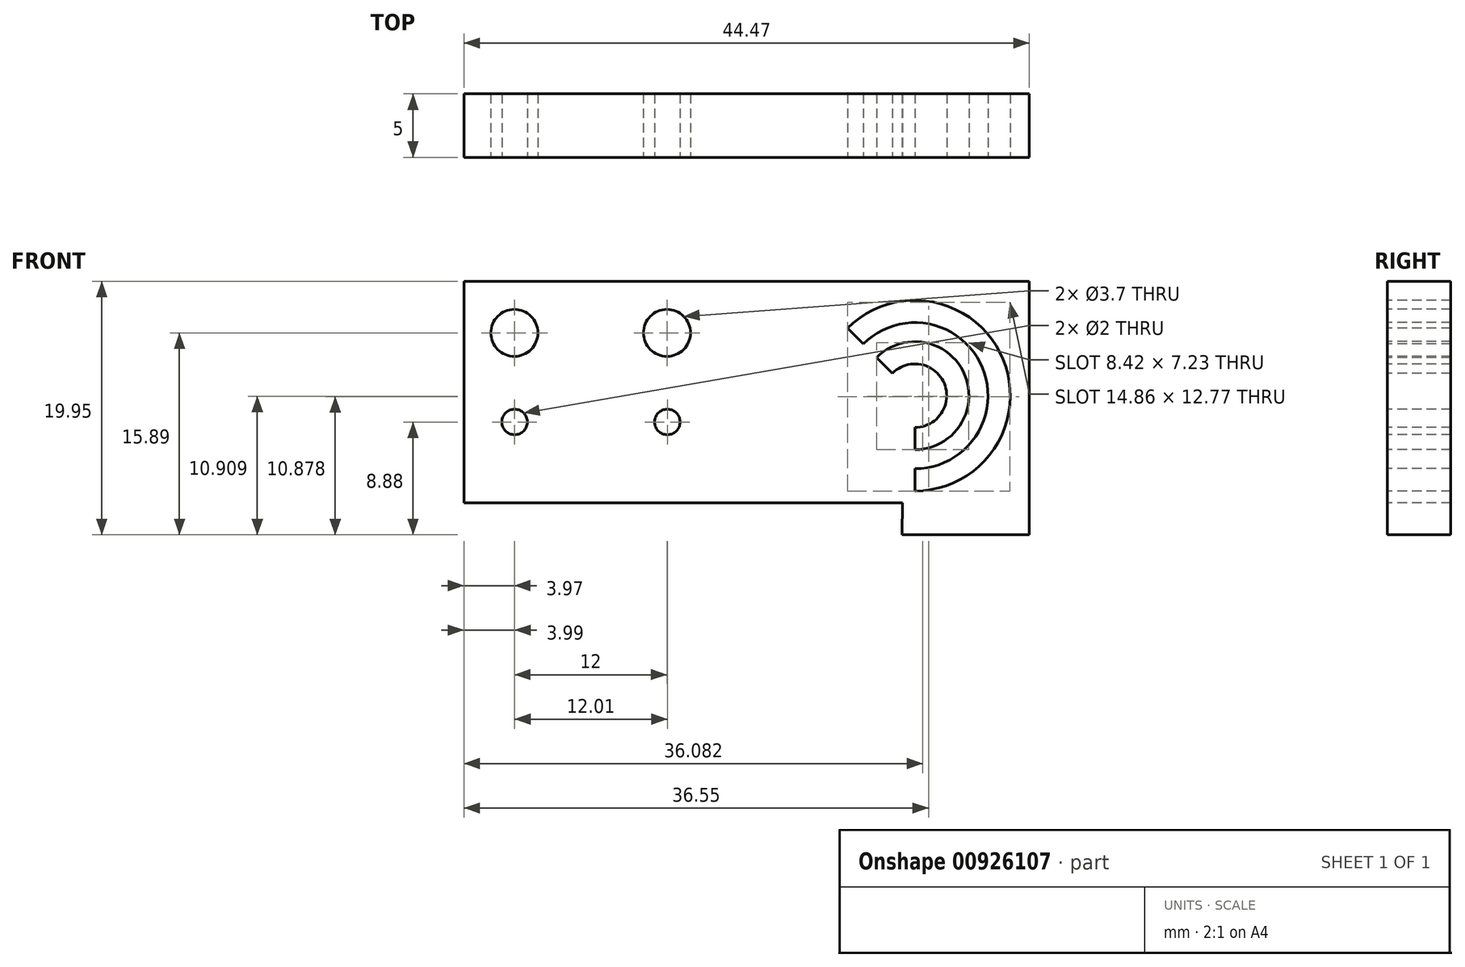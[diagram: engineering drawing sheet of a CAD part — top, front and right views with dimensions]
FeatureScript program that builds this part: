
annotation { "Feature Type Name" : "Feature", "Feature Type Description" : "" }
export const myFeature = defineFeature(function(context is Context, id is Id, definition is map)
    precondition{}
    {
        {
            var Q0;
            Q0=qCreatedBy(makeId("Front.planeOp"),FACE);
            var sketch = newSketch(context, id + "F0", { "sketchPlane" : qUnion([Q0])});
            skLineSegment(sketch, "E0", {"start": v(10, 19.95) * mm, "end": v(-34.47, 19.95) * mm});
            skLineSegment(sketch, "E1", {"start": v(-34.47, 2.5) * mm, "end": v(0.02, 2.5) * mm});
            skLineSegment(sketch, "E2", {"start": v(10, 19.95) * mm, "end": v(10, 0) * mm});
            skLineSegment(sketch, "E3", {"start": v(10, 0) * mm, "end": v(0, 0) * mm});
            skLineSegment(sketch, "E4", {"start": v(0, 0) * mm, "end": v(0.02, 2.5) * mm});
            skCircle(sketch, "E5", {"center": v(-30.5, 15.89) * mm, "radius": 1.85 * mm});
            skLineSegment(sketch, "E6", {"start": v(-34.47, 19.95) * mm, "end": v(-34.47, 2.5) * mm});
            skCircle(sketch, "E7", {"center": v(-18.5, 15.89) * mm, "radius": 1.85 * mm});
            skLineSegment(sketch, "E8", {"start": v(-34.47, 2.5) * mm, "end": v(-30.48, 2.5) * mm});
            skCircle(sketch, "E9", {"center": v(-30.48, 8.88) * mm, "radius": 1 * mm});
            skCircle(sketch, "E10", {"center": v(-18.47, 8.88) * mm, "radius": 1 * mm});
            skLineSegment(sketch, "E11", {"start": v(10, 19.95) * mm, "end": v(1, 19.95) * mm});
            skLineSegment(sketch, "E12", {"start": v(1, 19.95) * mm, "end": v(1, 10.95) * mm});
            skArc(sketch, "E13", {"start": v(1, 8.45) * mm, "mid": v(3.3, 11.9) * mm, "end": v(-0.77, 12.72) * mm});
            skArc(sketch, "E14", {"start": v(1, 6.7) * mm, "mid": v(4.93, 12.58) * mm, "end": v(-2, 13.96) * mm});
            skArc(sketch, "E15", {"start": v(1, 5.2) * mm, "mid": v(6.31, 13.15) * mm, "end": v(-3.07, 15.02) * mm});
            skArc(sketch, "E16", {"start": v(1, 3.45) * mm, "mid": v(7.93, 13.82) * mm, "end": v(-4.3, 16.25) * mm});
            skLineSegment(sketch, "E17", {"start": v(1, 8.45) * mm, "end": v(1, 6.7) * mm});
            skLineSegment(sketch, "E18", {"start": v(-0.77, 12.72) * mm, "end": v(-2, 13.96) * mm});
            skLineSegment(sketch, "E19.trimOffspring", {"start": v(-3.07, 15.02) * mm, "end": v(-4.3, 16.25) * mm});
            skLineSegment(sketch, "E20.trimOffspring", {"start": v(1, 5.2) * mm, "end": v(1, 3.45) * mm});
            skSolve(sketch);
        }
        {
            var Q0;
            Q0 = qSketchRegion(id + "F0", true);
            extrude(context, id + "F1", {"entities" : qUnion([Q0]), "oppositeDirection" : true, "depth" : 5 * mm, "offsetDistance" : 25 * mm});
        }
    });
